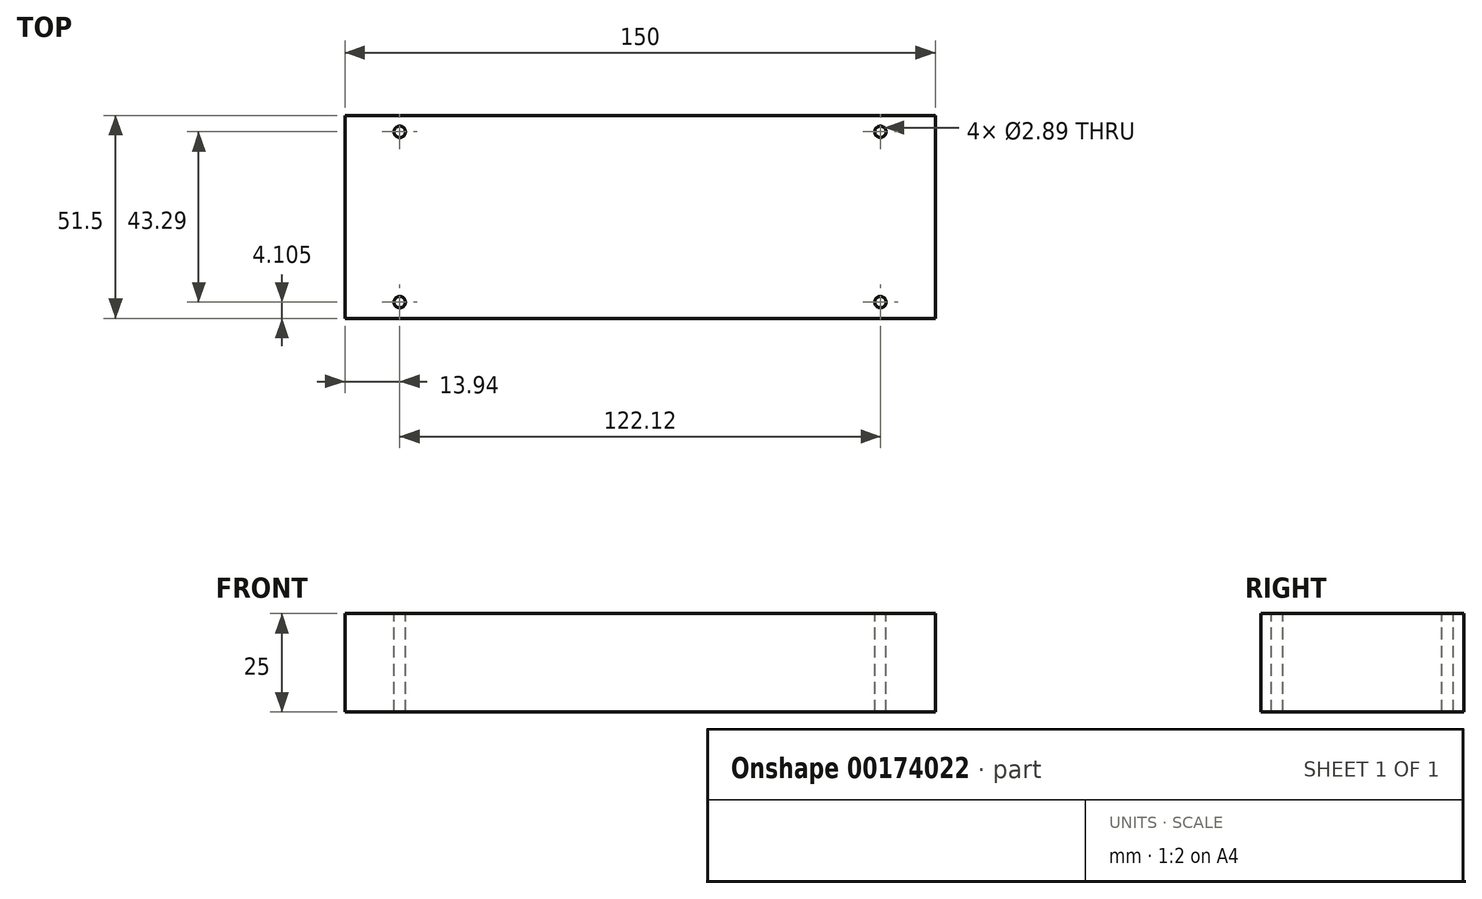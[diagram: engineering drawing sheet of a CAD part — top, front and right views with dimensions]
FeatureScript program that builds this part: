
annotation { "Feature Type Name" : "Feature", "Feature Type Description" : "" }
export const myFeature = defineFeature(function(context is Context, id is Id, definition is map)
    precondition{}
    {
        {
            var Q0;
            Q0=qCreatedBy(makeId("Top.planeOp"),FACE);
            var sketch = newSketch(context, id + "F0", { "sketchPlane" : qUnion([Q0])});
            skLineSegment(sketch, "E0.bottom", {"start": v(75, 25.75) * mm, "end": v(-75, 25.75) * mm});
            skLineSegment(sketch, "E0.top", {"start": v(75, -25.75) * mm, "end": v(-75, -25.75) * mm});
            skLineSegment(sketch, "E0.left", {"start": v(75, 25.75) * mm, "end": v(75, -25.75) * mm});
            skLineSegment(sketch, "E0.right", {"start": v(-75, 25.75) * mm, "end": v(-75, -25.75) * mm});
            skPoint(sketch, "E0.middle", {"position": v(0, 0) * mm});
            skSolve(sketch);
        }
        {
            var Q0;
            Q0 = qSketchRegion(id + "F0", true);
            extrude(context, id + "F1", {"entities" : qUnion([Q0]), "depth" : 25 * mm});
        }
        {
            var Q0;
            Q0=makeQuery(id+"F1.opExtrude","CAP_FACE",FACE,{"disambiguationData":[OSD([sQuery(id+"F0.wireOp",EDGE,"E0.bottom"),sQuery(id+"F0.wireOp",EDGE,"E0.top"),sQuery(id+"F0.wireOp",EDGE,"E0.left"),sQuery(id+"F0.wireOp",EDGE,"E0.right")])],"isStart":false});
            var sketch = newSketch(context, id + "F2", { "sketchPlane" : qUnion([Q0])});
            skLineSegment(sketch, "E1.bottom", {"start": v(61.06, 21.64) * mm, "end": v(-61.06, 21.64) * mm, "construction": true});
            skLineSegment(sketch, "E1.top", {"start": v(61.06, -21.64) * mm, "end": v(-61.06, -21.64) * mm, "construction": true});
            skLineSegment(sketch, "E1.left", {"start": v(61.06, 21.64) * mm, "end": v(61.06, -21.64) * mm, "construction": true});
            skLineSegment(sketch, "E1.right", {"start": v(-61.06, 21.64) * mm, "end": v(-61.06, -21.64) * mm, "construction": true});
            skPoint(sketch, "E1.middle", {"position": v(0, 0) * mm});
            skCircle(sketch, "E2", {"center": v(-61.06, 21.64) * mm, "radius": 1.45 * mm});
            skCircle(sketch, "E3", {"center": v(-61.06, -21.64) * mm, "radius": 1.45 * mm});
            skCircle(sketch, "E4", {"center": v(61.06, -21.64) * mm, "radius": 1.45 * mm});
            skCircle(sketch, "E5", {"center": v(61.06, 21.64) * mm, "radius": 1.45 * mm});
            skSolve(sketch);
        }
        {
            var Q0;
            Q0 = qSketchRegion(id + "F2", true);
            extrude(context, id + "F3", {"entities" : qUnion([Q0]), "operationType" : NewBodyOperationType.REMOVE, "endBound" : BoundingType.UP_TO_NEXT, "oppositeDirection" : true, "depth" : 25 * mm});
        }
    });
